# Revit family: Pantalla Modelo SF_SF10200W.1
name_source: partatom
category: Luminarias
units: mm (PartAtom-declared; Revit-internal decimal feet)

## family parameters
Compartido = No
Corte con vacíos al cargar = No
Cota de conector redondo = Diámetro de uso
Origen de luz = No
Punto de cálculo de habitación = No
Se basa en plano de trabajo = Sí
Siempre vertical = No
Tipo de pieza = Normal

## types (1)
- Pantalla Modelo SF_SF10200W.1
    Comentarios de vataje = 100-240V
    Descripción = PANTALLA MODELO SF10, PIXEL PITCH 10MM, RESOLUCION DE PANEL 128X32 DOTS, CANTIDAD/PANEL LED 10,000 DOTS, CONFIGURACION DE PIXEL SMD 3 EN 1, BRILLO 2000 NITS, FRECUENCIA DE ACTUALIZACION 3000Hz, ESCALA DE GRISES 16 BIT, AJUSTE DE BRILLO 256 NIVELES, CONTRASTE 2000:1, DIMENSION DEL PANEL 1280X320MM, PANEL 04096M2, PESO DEL PANEL 4.5kg, MAXIMO CONSUMO DE ENERGIA 200W, ANGULO DE VISUALIZACION 120 GRADOS EN HORIZONTAL Y VERTICAL, DISTANCIA DE VISUALIZACION 10M, TRANSPARENCIA 25%, PUNTO DE CONTROL <0.0002, DURACION DE LAS LUCES (50%  DE BRILLO) >50,000 HORAS, TEMPERATURA DE OPERACIÓN -10C +40C, HUMEDAD RELATIVA 10-90%, IP 43/54 (OPCIONAL), VOLTAJE AC 100-240V/50-60Hz, MODO DE ENTRADA CORRIENTE CONSTANTE, TIPO DE SEÑAL AV/S-VIDEO/VGA/CVBS/HDMI/DVI/SDI, DISTANCIA DE CONTROL HSYV <100M.
    Elevación por defecto = 0 mm  [stored 0 ft]
    Espesor = 1 mm  [stored 0.00328084 ft]
    Fabricante = BRILLANT
    Lámpara = SMD
    Modelo = SF10200W.1
    Modulo alto = 320 mm  [stored 1.04987 ft]
    Modulo largo = 1280 mm  [stored 4.19948 ft]
    Watt per fixture = 200

note: [stored X ft] marks values corroborated as IEEE doubles in the binary element streams (Revit-internal decimal feet)

## geometry (parser evidence)
native form markers: Blend x2
no freeform markers — native parametric forms only
